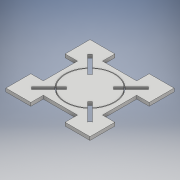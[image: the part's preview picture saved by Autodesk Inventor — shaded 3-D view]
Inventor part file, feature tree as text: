
AUTODESK INVENTOR PART (.ipt)
format: ipt  version: 2018 (Build 220112000, 112)  size: 209,408 bytes
history: native  units: mm
features: other x1, extrude x1, sketch x1
ambient origin geometry x8: Origin, YZ Plane, XZ Plane, XY Plane, X Axis, Y Axis, Z Axis, Center Point
bodies: Body1 (feature_tree)
feature tree (3):
  other  "Bryła1"
  extrude  "Wyciągnięcie proste1"  Depth=152.0mm
  sketch  "Szkic1"
